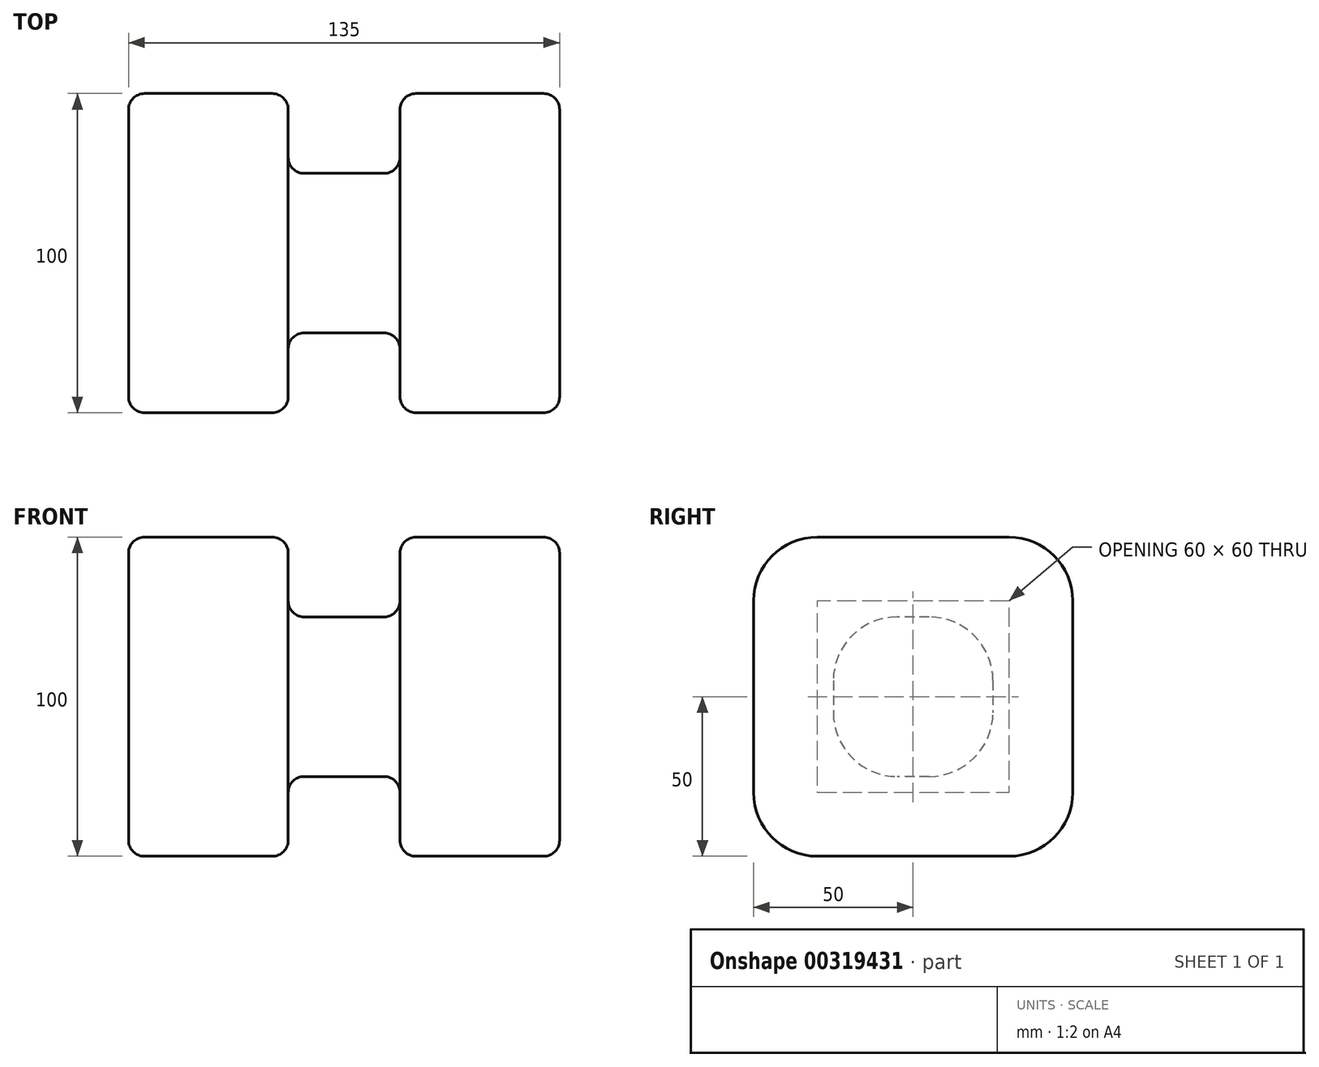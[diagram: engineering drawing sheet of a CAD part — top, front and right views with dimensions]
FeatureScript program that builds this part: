
annotation { "Feature Type Name" : "Feature", "Feature Type Description" : "" }
export const myFeature = defineFeature(function(context is Context, id is Id, definition is map)
    precondition{}
    {
        {
            var Q0;
            Q0=qCreatedBy(makeId("Right.planeOp"),FACE);
            var sketch = newSketch(context, id + "F0", { "sketchPlane" : qUnion([Q0])});
            skLineSegment(sketch, "E0.bottom", {"start": v(50, 50) * mm, "end": v(-50, 50) * mm});
            skLineSegment(sketch, "E0.top", {"start": v(50, -50) * mm, "end": v(-50, -50) * mm});
            skLineSegment(sketch, "E0.left", {"start": v(50, 50) * mm, "end": v(50, -50) * mm});
            skLineSegment(sketch, "E0.right", {"start": v(-50, 50) * mm, "end": v(-50, -50) * mm});
            skPoint(sketch, "E0.middle", {"position": v(0, 0) * mm});
            skSolve(sketch);
        }
        {
            var Q0;
            Q0=makeQuery(id+"F0.imprint","IMPRINT",FACE,{"disambiguationData":[TD([[makeQuery(id+"F0.imprint","IMPRINT",EDGE,{"derivedFrom":sQuery(id+"F0.wireOp",EDGE,"E0.bottom")}),1.0]])]});
            extrude(context, id + "F1", {"entities" : qUnion([Q0]), "depth" : 50 * mm});
        }
        {
            var Q0;
            Q0=makeQuery(id+"F1.opExtrude","CAP_FACE",FACE,{"disambiguationData":[OSD([sQuery(id+"F0.wireOp",EDGE,"E0.bottom"),sQuery(id+"F0.wireOp",EDGE,"E0.top"),sQuery(id+"F0.wireOp",EDGE,"E0.left"),sQuery(id+"F0.wireOp",EDGE,"E0.right")])],"isStart":false});
            var sketch = newSketch(context, id + "F2", { "sketchPlane" : qUnion([Q0])});
            skLineSegment(sketch, "E1.bottom", {"start": v(25, 25) * mm, "end": v(-25, 25) * mm});
            skLineSegment(sketch, "E1.top", {"start": v(25, -25) * mm, "end": v(-25, -25) * mm});
            skLineSegment(sketch, "E1.left", {"start": v(25, 25) * mm, "end": v(25, -25) * mm});
            skLineSegment(sketch, "E1.right", {"start": v(-25, 25) * mm, "end": v(-25, -25) * mm});
            skPoint(sketch, "E1.middle", {"position": v(0, 0) * mm});
            skSolve(sketch);
        }
        {
            var Q0;
            Q0=makeQuery(id+"F2.imprint","IMPRINT",FACE,{"disambiguationData":[TD([[makeQuery(id+"F2.imprint","IMPRINT",EDGE,{"derivedFrom":sQuery(id+"F2.wireOp",EDGE,"E1.bottom")}),1.0]])]});
            extrude(context, id + "F3", {"entities" : qUnion([Q0]), "operationType" : NewBodyOperationType.ADD, "depth" : 35 * mm});
        }
        {
            var Q0;
            Q0=makeQuery(id+"F3.opExtrude","CAP_FACE",FACE,{"disambiguationData":[OSD([sQuery(id+"F2.wireOp",EDGE,"E1.bottom"),sQuery(id+"F2.wireOp",EDGE,"E1.top"),sQuery(id+"F2.wireOp",EDGE,"E1.left"),sQuery(id+"F2.wireOp",EDGE,"E1.right")])],"isStart":false});
            var sketch = newSketch(context, id + "F4", { "sketchPlane" : qUnion([Q0])});
            skLineSegment(sketch, "E2.0.0", {"start": v(-50, -50) * mm, "end": v(50, -50) * mm});
            skLineSegment(sketch, "E2.0.1", {"start": v(50, -50) * mm, "end": v(50, 50) * mm});
            skLineSegment(sketch, "E2.0.2", {"start": v(50, 50) * mm, "end": v(-50, 50) * mm});
            skLineSegment(sketch, "E2.0.3", {"start": v(-50, 50) * mm, "end": v(-50, -50) * mm});
            skSolve(sketch);
        }
        {
            var Q0;
            Q0 = qSketchRegion(id + "F4", true);
            extrude(context, id + "F5", {"entities" : qUnion([Q0]), "operationType" : NewBodyOperationType.ADD, "depth" : 50 * mm});
        }
        {
            var Q0;
            Q0=makeQuery(id+"F5.opExtrude","SWEPT_EDGE",EDGE,{"disambiguationData":[OSD([sQuery(id+"F4.wireOp",EDGE,"E2.0.0"),sQuery(id+"F4.wireOp",EDGE,"E2.0.1")])]});
            var Q1;
            Q1=makeQuery(id+"F1.opExtrude","SWEPT_EDGE",EDGE,{"disambiguationData":[OSD([sQuery(id+"F0.wireOp",EDGE,"E0.top"),sQuery(id+"F0.wireOp",EDGE,"E0.left")])]});
            var Q2;
            Q2=makeQuery(id+"F1.opExtrude","SWEPT_EDGE",EDGE,{"disambiguationData":[OSD([sQuery(id+"F0.wireOp",EDGE,"E0.bottom"),sQuery(id+"F0.wireOp",EDGE,"E0.left")])]});
            var Q3;
            Q3=makeQuery(id+"F5.opExtrude","SWEPT_EDGE",EDGE,{"disambiguationData":[OSD([sQuery(id+"F4.wireOp",EDGE,"E2.0.1"),sQuery(id+"F4.wireOp",EDGE,"E2.0.2")])]});
            var Q4;
            Q4=makeQuery(id+"F1.opExtrude","SWEPT_EDGE",EDGE,{"disambiguationData":[OSD([sQuery(id+"F0.wireOp",EDGE,"E0.top"),sQuery(id+"F0.wireOp",EDGE,"E0.right")])]});
            var Q5;
            Q5=makeQuery(id+"F5.opExtrude","SWEPT_EDGE",EDGE,{"disambiguationData":[OSD([sQuery(id+"F4.wireOp",EDGE,"E2.0.0"),sQuery(id+"F4.wireOp",EDGE,"E2.0.3")])]});
            var Q6;
            Q6=makeQuery(id+"F1.opExtrude","SWEPT_EDGE",EDGE,{"disambiguationData":[OSD([sQuery(id+"F0.wireOp",EDGE,"E0.bottom"),sQuery(id+"F0.wireOp",EDGE,"E0.right")])]});
            var Q7;
            Q7=makeQuery(id+"F5.opExtrude","SWEPT_EDGE",EDGE,{"disambiguationData":[OSD([sQuery(id+"F4.wireOp",EDGE,"E2.0.2"),sQuery(id+"F4.wireOp",EDGE,"E2.0.3")])]});
            var Q8;
            Q8=makeQuery(id+"F3.opExtrude","SWEPT_EDGE",EDGE,{"disambiguationData":[OSD([sQuery(id+"F2.wireOp",EDGE,"E1.top"),sQuery(id+"F2.wireOp",EDGE,"E1.left")])]});
            var Q9;
            Q9=makeQuery(id+"F3.opExtrude","SWEPT_EDGE",EDGE,{"disambiguationData":[OSD([sQuery(id+"F2.wireOp",EDGE,"E1.bottom"),sQuery(id+"F2.wireOp",EDGE,"E1.left")])]});
            var Q10;
            Q10=makeQuery(id+"F3.opExtrude","SWEPT_EDGE",EDGE,{"disambiguationData":[OSD([sQuery(id+"F2.wireOp",EDGE,"E1.top"),sQuery(id+"F2.wireOp",EDGE,"E1.right")])]});
            var Q11;
            Q11=makeQuery(id+"F3.opExtrude","SWEPT_EDGE",EDGE,{"disambiguationData":[OSD([sQuery(id+"F2.wireOp",EDGE,"E1.bottom"),sQuery(id+"F2.wireOp",EDGE,"E1.right")])]});
            fillet(context, id + "F6", {"entities" : qUnion([Q0, Q1, Q2, Q3, Q4, Q5, Q6, Q7, Q8, Q9, Q10, Q11]), "radius" : 20 * mm, "tangentPropagation" : true, "allowEdgeOverflow" : false});
        }
        {
            var Q0;
            Q0=makeQuery(id+"F6.opFillet","BLEND_EDGE",EDGE,{"blendedFrom":[makeQuery(id+"F3.opExtrude","SWEPT_EDGE",EDGE,{"disambiguationData":[OSD([sQuery(id+"F2.wireOp",EDGE,"E1.bottom"),sQuery(id+"F2.wireOp",EDGE,"E1.right")])]}),makeQuery(id+"F1.opExtrude","CAP_FACE",FACE,{"disambiguationData":[OSD([sQuery(id+"F0.wireOp",EDGE,"E0.bottom"),sQuery(id+"F0.wireOp",EDGE,"E0.top"),sQuery(id+"F0.wireOp",EDGE,"E0.left"),sQuery(id+"F0.wireOp",EDGE,"E0.right")])],"isStart":false})],"blendedInto":[makeQuery(id+"F1.opExtrude","CAP_FACE",FACE,{"disambiguationData":[OSD([sQuery(id+"F0.wireOp",EDGE,"E0.bottom"),sQuery(id+"F0.wireOp",EDGE,"E0.top"),sQuery(id+"F0.wireOp",EDGE,"E0.left"),sQuery(id+"F0.wireOp",EDGE,"E0.right")])],"isStart":false})]});
            var Q1;
            Q1=makeQuery(id+"F1.opExtrude","CAP_EDGE",EDGE,{"disambiguationData":[OSD([sQuery(id+"F0.wireOp",EDGE,"E0.right")])],"isStart":false});
            var Q2;
            Q2=makeQuery(id+"F5.opExtrude","CAP_EDGE",EDGE,{"disambiguationData":[OSD([sQuery(id+"F4.wireOp",EDGE,"E2.0.3")])],"isStart":true});
            var Q3;
            Q3=makeQuery(id+"F5.opExtrude","CAP_EDGE",EDGE,{"disambiguationData":[OSD([sQuery(id+"F4.wireOp",EDGE,"E2.0.3")])],"isStart":false});
            var Q4;
            Q4=makeQuery(id+"F1.opExtrude","CAP_EDGE",EDGE,{"disambiguationData":[OSD([sQuery(id+"F0.wireOp",EDGE,"E0.right")])],"isStart":true});
            var Q5;
            Q5=makeQuery(id+"F6.opFillet","BLEND_EDGE",EDGE,{"blendedFrom":[makeQuery(id+"F3.opExtrude","SWEPT_EDGE",EDGE,{"disambiguationData":[OSD([sQuery(id+"F2.wireOp",EDGE,"E1.bottom"),sQuery(id+"F2.wireOp",EDGE,"E1.right")])]}),makeQuery(id+"F5.opExtrude","CAP_FACE",FACE,{"disambiguationData":[OSD([sQuery(id+"F4.wireOp",EDGE,"E2.0.0"),sQuery(id+"F4.wireOp",EDGE,"E2.0.1"),sQuery(id+"F4.wireOp",EDGE,"E2.0.2"),sQuery(id+"F4.wireOp",EDGE,"E2.0.3")])],"isStart":true})],"blendedInto":[makeQuery(id+"F5.opExtrude","CAP_FACE",FACE,{"disambiguationData":[OSD([sQuery(id+"F4.wireOp",EDGE,"E2.0.0"),sQuery(id+"F4.wireOp",EDGE,"E2.0.1"),sQuery(id+"F4.wireOp",EDGE,"E2.0.2"),sQuery(id+"F4.wireOp",EDGE,"E2.0.3")])],"isStart":true})]});
            fillet(context, id + "F7", {"entities" : qUnion([Q0, Q1, Q2, Q3, Q4, Q5]), "radius" : 5 * mm, "tangentPropagation" : true, "allowEdgeOverflow" : false});
        }
    });
